# Revit family: Electronics_Commercial-Loudspeakers_Dual-Coil-Ceiling-Subwoofer_CMSUB8
name_source: partatom
category: Communication Devices
units: mm (PartAtom-declared; Revit-internal decimal feet)

## family parameters
Cut with Voids When Loaded = No
Host = Face
Maintain Annotation Orientation = No
OmniClass Number = 23.85.10.11.14.14.14
OmniClass Title = Loudspeakers
Part Type = Normal
Room Calculation Point = No
Round Connector Dimension = Use Diameter
Shared = No

## types (1)
- CMSUB8
    Applicable low impedance = Yes
    Closest RAL colour (subject to deviations) = RAL9010
    Colour = White
    Connector Description = Terminal strip; Low impedance 2 x 8 ohms
    Cutout in mm = 223
    Default Elevation = 4' - 0"
    Depth = 0' - 4"
    Description = CMSUB8 8 Dual Coil Ceiling Subwoofer
    Diameter = 0' - 9 1/2"
    Frequency response in Hz = 50 - 200
    Grill Material = Biamp - Plastic - White(Grid)
    Grille main material = Aluminium
    Housing Material = Biamp - Plastic - White
    IP rating = 54
    Impedance in ohms = 2 x 8
    Installation grip range in mm = 3 - 28
    Loudspeaker system = Dual coil
    Low impedance RMS power in watts = 2 x 40
    Low impedance dynamic power in watts = 2 x 80
    Main construction material = ABS plastic
    Manufacturer = Biamp
    Max SPL 1m in dB = 107
    Model = CMSUB8
    Mounting system = 3 screws
    Product Documentation Link = https://downloads.biamp.com
    Product Page URL = https://www.biamp.com
    Product data url = https://bimobject.com
    SPL 1W/1m in dB = 88
    Tweeter size in inch = 1
    URL = https://www.biamp.com
    Vertical dispersion angle 1000 Hz = 180°
    Weight = 4.63 lb
    Woofer cone material = Coated paper
    Woofer size in inch = 8

## geometry (parser evidence)
native form markers: Sweep x2
no freeform markers — native parametric forms only
